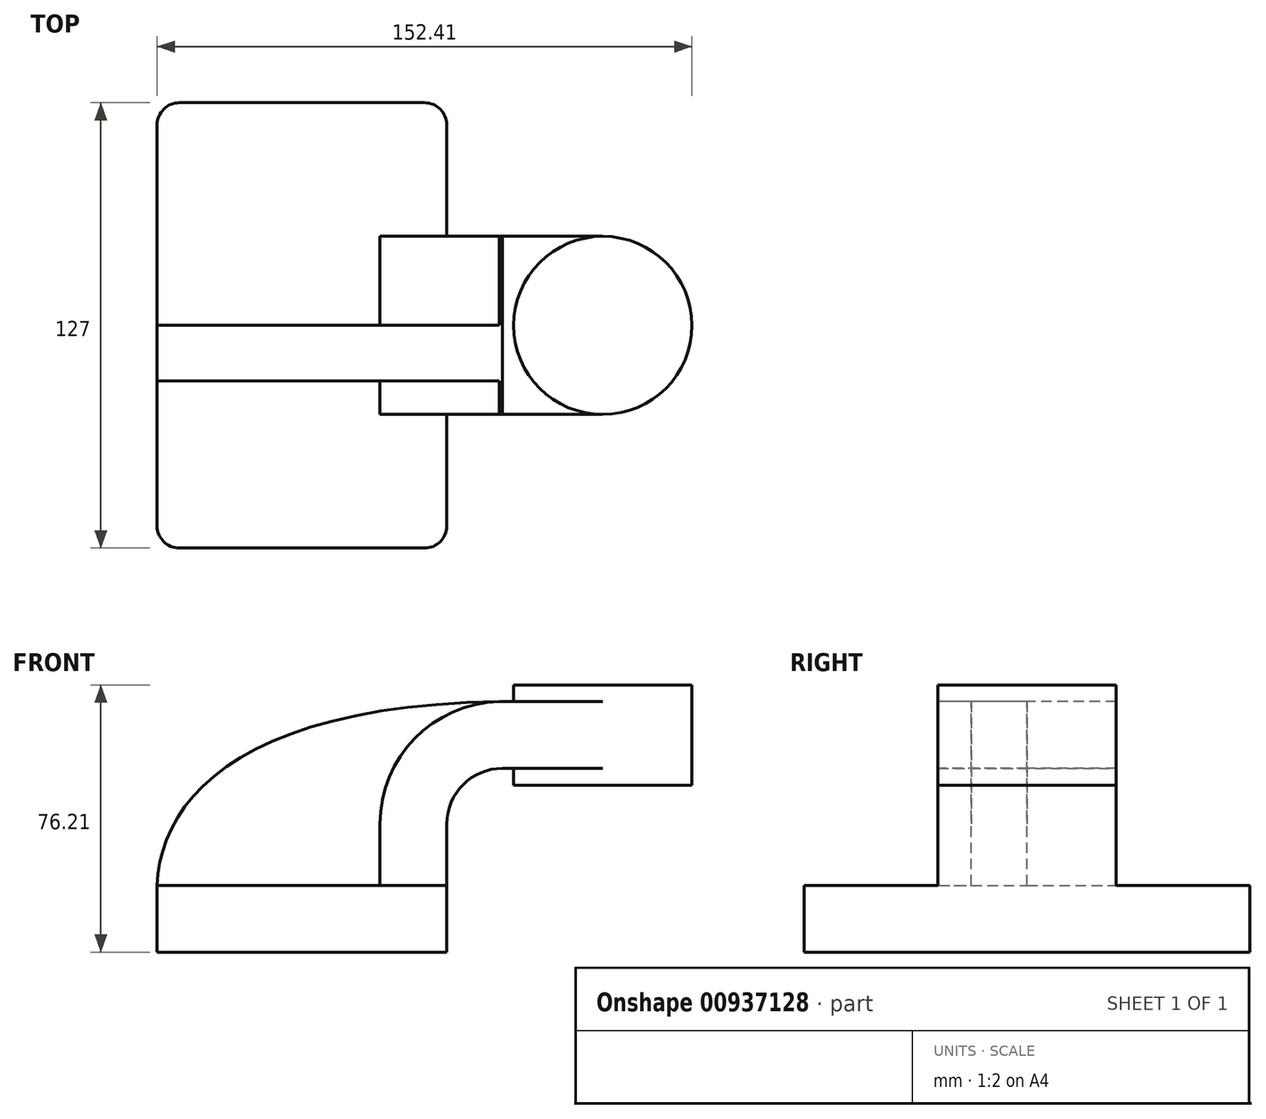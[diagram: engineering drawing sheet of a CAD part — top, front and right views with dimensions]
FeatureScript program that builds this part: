
annotation { "Feature Type Name" : "Feature", "Feature Type Description" : "" }
export const myFeature = defineFeature(function(context is Context, id is Id, definition is map)
    precondition{}
    {
        {
            var Q0;
            Q0=qCreatedBy(makeId("Front.planeOp"),FACE);
            var sketch = newSketch(context, id + "F0", { "sketchPlane" : qUnion([Q0])});
            skLineSegment(sketch, "E0.bottom", {"start": v(-41.28, -9.52) * mm, "end": v(41.28, -9.52) * mm});
            skLineSegment(sketch, "E0.top", {"start": v(-41.28, 9.53) * mm, "end": v(41.27, 9.53) * mm});
            skLineSegment(sketch, "E0.left", {"start": v(-41.27, -9.52) * mm, "end": v(-41.28, 9.53) * mm});
            skLineSegment(sketch, "E0.right", {"start": v(41.28, -9.52) * mm, "end": v(41.27, 9.53) * mm});
            skPoint(sketch, "E0.middle", {"position": v(0, 0) * mm});
            skLineSegment(sketch, "E1.bottom", {"start": v(60.32, 38.1) * mm, "end": v(111.12, 38.1) * mm});
            skLineSegment(sketch, "E1.top", {"start": v(60.32, 66.68) * mm, "end": v(111.12, 66.68) * mm});
            skLineSegment(sketch, "E1.left", {"start": v(60.32, 38.1) * mm, "end": v(60.32, 66.68) * mm});
            skLineSegment(sketch, "E1.right", {"start": v(111.12, 38.1) * mm, "end": v(111.12, 66.68) * mm});
            skPoint(sketch, "E1.middle", {"position": v(85.72, 52.39) * mm});
            skLineSegment(sketch, "E2", {"start": v(41.27, 9.52) * mm, "end": v(41.27, 27) * mm});
            skArc(sketch, "E3", {"start": v(57.15, 42.88) * mm, "mid": v(45.92, 38.23) * mm, "end": v(41.27, 27) * mm});
            skLineSegment(sketch, "E4", {"start": v(57.15, 42.88) * mm, "end": v(93.93, 42.88) * mm});
            skLineSegment(sketch, "E5.0", {"start": v(57.15, 61.93) * mm, "end": v(93.93, 61.93) * mm});
            skArc(sketch, "E5.1", {"start": v(57.15, 61.93) * mm, "mid": v(32.45, 51.7) * mm, "end": v(22.22, 27) * mm});
            skLineSegment(sketch, "E5.2", {"start": v(22.22, 9.52) * mm, "end": v(22.22, 27) * mm});
            skLineSegment(sketch, "E6", {"start": v(85.72, 38.1) * mm, "end": v(85.72, 66.68) * mm});
            skFitSpline(sketch, "E7", {"points": [v(-41.28, 9.53) * mm, v(57.15, 61.93) * mm], "startDerivative": vector(2.93, 74.79) * mm, "endDerivative": vector(221.48, 2.56) * mm});
            skSolve(sketch);
        }
        {
            var Q0;
            Q0=makeQuery(id+"F0.imprint","IMPRINT",FACE,{"disambiguationData":[TD([[makeQuery(id+"F0.imprint","IMPRINT",EDGE,{"derivedFrom":sQuery(id+"F0.wireOp",EDGE,"E0.bottom")}),1.0]])]});
            extrude(context, id + "F1", {"entities" : qUnion([Q0]), "endBound" : BoundingType.SYMMETRIC, "depth" : 127 * mm, "offsetDistance" : 25.4 * mm});
        }
        {
            var Q0;
            {var subQ1=sQuery(id+"F0.wireOp",EDGE,"E2");Q0=makeQuery(id+"F0.imprint","IMPRINT",FACE,{"disambiguationData":[TD([[makeQuery(id+"F0.imprint","IMPRINT",EDGE,{"derivedFrom":subQ1}),1.0]])]});}
            var Q1;
            {var subQ0=sQuery(id+"F0.wireOp",EDGE,"E4");var subQ1=sQuery(id+"F0.wireOp",EDGE,"E1.left");var subQ2=makeQuery(id+"F0.imprint","INTERSECT",VERTEX,{"derivedFrom":[subQ1,subQ0]});Q1=makeQuery(id+"F0.imprint","IMPRINT",FACE,{"disambiguationData":[TD([[makeQuery(id+"F0.imprint","IMPRINT",EDGE,{"disambiguationData":[TD([[subQ2,-1.0]])],"derivedFrom":subQ1}),-1.0]])]});}
            extrude(context, id + "F2", {"entities" : qUnion([Q0, Q1]), "operationType" : NewBodyOperationType.ADD, "endBound" : BoundingType.SYMMETRIC, "depth" : 50.8 * mm, "offsetDistance" : 25.4 * mm});
        }
        {
            var Q0;
            {var subQ3=sQuery(id+"F0.wireOp",EDGE,"E5.2");Q0=makeQuery(id+"F0.imprint","IMPRINT",FACE,{"disambiguationData":[TD([[makeQuery(id+"F0.imprint","IMPRINT",EDGE,{"derivedFrom":subQ3}),1.0]])]});}
            extrude(context, id + "F3", {"entities" : qUnion([Q0]), "operationType" : NewBodyOperationType.ADD, "depth" : 15.88 * mm, "offsetDistance" : 25.4 * mm});
        }
        {
            var Q0;
            {var subQ4=sQuery(id+"F0.wireOp",EDGE,"E1.right");Q0=makeQuery(id+"F0.imprint","IMPRINT",FACE,{"disambiguationData":[TD([[makeQuery(id+"F0.imprint","IMPRINT",EDGE,{"derivedFrom":subQ4}),1.0]])]});}
            var Q1;
            Q1=sQuery(id+"F0.wireOp",EDGE,"E6");
            revolve(context, id + "F4", {"operationType" : NewBodyOperationType.ADD, "surfaceOperationType" : NewSurfaceOperationType.NEW, "entities" : qUnion([Q0]), "axis" : qUnion([Q1]), "revolveType" : RevolveType.FULL});
        }
        {
            var Q0;
            Q0=makeQuery(id+"F1.opExtrude","CAP_EDGE",EDGE,{"disambiguationData":[OSD([sQuery(id+"F0.wireOp",EDGE,"E0.right")])],"isStart":false});
            var Q1;
            Q1=makeQuery(id+"F1.opExtrude","CAP_EDGE",EDGE,{"disambiguationData":[OSD([sQuery(id+"F0.wireOp",EDGE,"E0.left")])],"isStart":false});
            var Q2;
            Q2=makeQuery(id+"F1.opExtrude","CAP_EDGE",EDGE,{"disambiguationData":[OSD([sQuery(id+"F0.wireOp",EDGE,"E0.right")])],"isStart":true});
            var Q3;
            Q3=makeQuery(id+"F1.opExtrude","CAP_EDGE",EDGE,{"disambiguationData":[OSD([sQuery(id+"F0.wireOp",EDGE,"E0.left")])],"isStart":true});
            fillet(context, id + "F5", {"entities" : qUnion([Q0, Q1, Q2, Q3]), "radius" : 6.35 * mm, "tangentPropagation" : true, "allowEdgeOverflow" : false});
        }
    });
